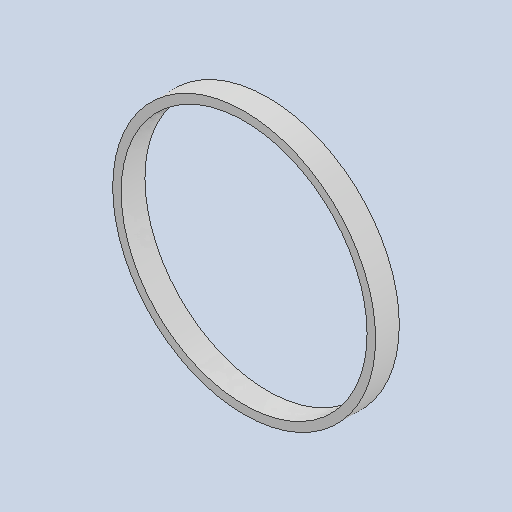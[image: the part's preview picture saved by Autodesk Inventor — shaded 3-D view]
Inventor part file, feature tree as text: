
AUTODESK INVENTOR PART (.ipt)
format: ipt  version: 2024.2 (Build 282272000, 272)  size: 246,784 bytes
history: native  units: mm
features: extrude x1, sketch x1
ambient origin geometry x8: Origin, YZ Plane, XZ Plane, XY Plane, X Axis, Y Axis, Z Axis, Center Point
bodies: Solid1 (feature_tree)
feature tree (2):
  extrude  "Extrusion1"  Depth=28.0mm
  sketch  "Sketch1"  dims[d0=10.0mm d1=290.0mm d2=28.0mm d3=0.0mm]
